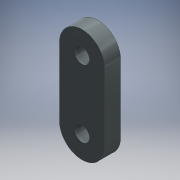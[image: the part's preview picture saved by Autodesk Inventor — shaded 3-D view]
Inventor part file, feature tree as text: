
AUTODESK INVENTOR PART (.ipt)
format: ipt  version: 2016 (Build 200138000, 138)  size: 118,272 bytes
history: native  units: mm
features: extrude x1, sketch x1
ambient origin geometry x8: Origin, YZ Plane, XZ Plane, XY Plane, X Axis, Y Axis, Z Axis, Center Point
bodies: Solid1 (feature_tree)
feature tree (2):
  extrude  "Extrusion1"  Depth=3.0mm
  sketch  "Sketch1"  dims[d0=8.5mm d2=2.8mm d3=2.8mm d7=4.25mm d10=4.25mm d11=12.7mm d12=0.0mm d13=3.0mm d14=0.0mm]
